# Revit family: NBS_TapcoRoofingProducts_RcnstttdSltCrsngFitngs_TapcoSlate_ClassicRidgeEndCap
name_source: partatom
category: Generic Models
units: mm (PartAtom-declared; Revit-internal decimal feet)

## family parameters
Can host rebar = No
Cut with Voids When Loaded = No
Part Type = Normal
Room Calculation Point = No
Round Connector Dimension = Use Diameter
Shared = No

## types (15) — shared parameters
Applications = Suitable for Tapco Slate Classic and Tapco Slate Classic Ridge and Hip Caps
AssetType = Fixed
Category = Pr_25_93_72_73:Reconstituted slate coursing fittings
ClassicRidgeEndCapHeight = 98 mm  [stored 0.321522 ft]
ClassicRidgeEndCapMaterial = NBS_TapcoRoofingProducts_Slate_706Plum
CodePerformance = Fully tested to BBA, ETA and CE standards
Combustible = Yes
Description = A dry-fix ridge 90° end cap to weather seal and finish the roof line at the end of the ridge, manufactured in the same material as our Tapco Slate Classic product to match the roof slate
DurationUnit = year
ExpectedLife = 80+ years
Features = Lightweight – as low as 12 kg per square metre, easy to install with pre-marked nailing guides and spacers, easily cut with a fine-toothed saw or sharp utility blade, mechanically fixed
FireRating = BS476 Part 3, Boarded Roof SAA, Battened Roof SAC
FlammabilityRating = BS476 Part 3, Boarded Roof SAA, Battened Roof SAC
IfcExportAs = IfcCoveringType
IfcExportType = ROOFING
IsExternal = Yes
ManufacturerName = Tapco Roofing Products
ManufacturerURL = www.tapcoroofingproducts.com
Material = Virgin limestone, polypropylene
NBSCertification = www.nationalbimlibrary.com/cert/mlktdb3y
NBSDescription = Reconstituted slates coursing fittings
NBSReference = 45-80-90/388
NominalHeight = 70 mm
NominalLength = 445 mm  [stored 1.45997 ft]
NominalWidth = 290 mm
ProductInformation = https://www.tapcoroofingproducts.com
Shape = Rectangular
Size = 70 x 445 x 290 mm
Status = UNSET
Uniclass2015Code = Pr_25_93_72_73
Uniclass2015Title = Reconstituted slate coursing fittings
Uniclass2015Version = Products v1.20
Version = 1
WarrantyDescription = 40-years
WarrantyDurationUnit = year
zero-valued in all types: ThermalTransmittance

## per-type parameters (varying)
| type | BIMObjectName | Color | Colour | EndCapPitchAngle | ModelNumber | Name | PitchRange |
| TapcoSlate_ClassicRidgeEndCap_804PewterGrey_25To29DegPitch | NBS_TapcoRoofingProducts_ReconstitutedSlatesCoursingFittings_TapcoSlate_ClassicRidgeEndCap_804PewterGrey_25To29DegPitch | Pewter grey | Pewter grey | 25.00° | 804 | ReconstitutedSlatesCoursingFittings_TapcoSlate_ClassicRidgeEndCap_804PewterGrey_25To29DegPitch_TapcoRoofingProducts | 25° - 29° |
| TapcoSlate_ClassicRidgeEndCap_804PewterGrey30To34DegPitch | NBS_TapcoRoofingProducts_ReconstitutedSlatesCoursingFittings_TapcoSlate_ClassicRidgeEndCap_804PewterGrey30To34DegPitch | Pewter grey | Pewter grey | 30.00° | 804 | ReconstitutedSlatesCoursingFittings_TapcoSlate_ClassicRidgeEndCap_804PewterGrey30To34DegPitch_TapcoRoofingProducts | 30° - 34° |
| TapcoSlate_ClassicRidgeEndCap_804PewterGrey35To40DegPitch | NBS_TapcoRoofingProducts_ReconstitutedSlatesCoursingFittings_TapcoSlate_ClassicRidgeEndCap_804PewterGrey35To40DegPitch | Pewter grey | Pewter grey | 35.00° | 804 | ReconstitutedSlatesCoursingFittings_TapcoSlate_ClassicRidgeEndCap_804PewterGrey35To40DegPitch_TapcoRoofingProducts | 35° - 40° |
| TapcoSlate_ClassicRidgeEndCap_809RedRock_25To29DegPitch | NBS_TapcoRoofingProducts_ReconstitutedSlatesCoursingFittings_TapcoSlate_ClassicRidgeEndCap_809RedRock_25To29DegPitch | Red rock | Red rock | 25.00° | 809 | ReconstitutedSlatesCoursingFittings_TapcoSlate_ClassicRidgeEndCap_809RedRock_25To29DegPitch_TapcoRoofingProducts | 25° - 29° |
| TapcoSlate_ClassicRidgeEndCap_809RedRock_30To34DegPitch | NBS_TapcoRoofingProducts_ReconstitutedSlatesCoursingFittings_TapcoSlate_ClassicRidgeEndCap_809RedRock_30To34DegPitch | Red rock | Red rock | 30.00° | 809 | ReconstitutedSlatesCoursingFittings_TapcoSlate_ClassicRidgeEndCap_809RedRock_30To34DegPitch_TapcoRoofingProducts | 30° - 34° |
| TapcoSlate_ClassicRidgeEndCap_809RedRock_35To40DegPitch | NBS_TapcoRoofingProducts_ReconstitutedSlatesCoursingFittings_TapcoSlate_ClassicRidgeEndCap_809RedRock_35To40DegPitch | Red rock | Red rock | 35.00° | 809 | ReconstitutedSlatesCoursingFittings_TapcoSlate_ClassicRidgeEndCap_809RedRock_35To40DegPitch_TapcoRoofingProducts | 35° - 40° |
| TapcoSlate_ClassicRidgeEndCap_706Plum_25To29DegPitch | NBS_TapcoRoofingProducts_ReconstitutedSlatesCoursingFittings_TapcoSlate_ClassicRidgeEndCap_706Plum_25To29DegPitch | Plum | Plum | 25.00° | 706 | ReconstitutedSlatesCoursingFittings_TapcoSlate_ClassicRidgeEndCap_706Plum_25To29DegPitch_TapcoRoofingProducts | 25° - 29° |
| TapcoSlate_ClassicRidgeEndCap_706Plum_30To34DegPitch | NBS_TapcoRoofingProducts_ReconstitutedSlatesCoursingFittings_TapcoSlate_ClassicRidgeEndCap_706Plum_30To34DegPitch | Plum | Plum | 30.00° | 706 | ReconstitutedSlatesCoursingFittings_TapcoSlate_ClassicRidgeEndCap_706Plum_30To34DegPitch_TapcoRoofingProducts | 30° - 34° |
| TapcoSlate_ClassicRidgeEndCap_706Plum_35To40DegPitch | NBS_TapcoRoofingProducts_ReconstitutedSlatesCoursingFittings_TapcoSlate_ClassicRidgeEndCap_706Plum_35To40DegPitch | Plum | Plum | 35.00° | 706 | ReconstitutedSlatesCoursingFittings_TapcoSlate_ClassicRidgeEndCap_706Plum_35To40DegPitch_TapcoRoofingProducts | 35° - 40° |
| TapcoSlate_ClassicRidgeEndCap_709BrickRed_25To29DegPitch | NBS_TapcoRoofingProducts_ReconstitutedSlatesCoursingFittings_TapcoSlate_ClassicRidgeEndCap_709BrickRed_25To29DegPitch | Brick red | Brick red | 25.00° | 709 | ReconstitutedSlatesCoursingFittings_TapcoSlate_ClassicRidgeEndCap_709BrickRed_25To29DegPitch_TapcoRoofingProducts | 25° - 29° |
| TapcoSlate_ClassicRidgeEndCap_709BrickRed_30To34DegPitch | NBS_TapcoRoofingProducts_ReconstitutedSlatesCoursingFittings_TapcoSlate_ClassicRidgeEndCap_709BrickRed_30To34DegPitch | Brick red | Brick red | 30.00° | 709 | ReconstitutedSlatesCoursingFittings_TapcoSlate_ClassicRidgeEndCap_709BrickRed_30To34DegPitch_TapcoRoofingProducts | 30° - 34° |
| TapcoSlate_ClassicRidgeEndCap_709BrickRed_35To40DegPitch | NBS_TapcoRoofingProducts_ReconstitutedSlatesCoursingFittings_TapcoSlate_ClassicRidgeEndCap_709BrickRed_35To40DegPitch | Brick red | Brick red | 35.00° | 709 | ReconstitutedSlatesCoursingFittings_TapcoSlate_ClassicRidgeEndCap_709BrickRed_35To40DegPitch_TapcoRoofingProducts | 35° - 40° |
| TapcoSlate_ClassicRidgeEndCap_712ChestnutBrown_25To29DegPitch | NBS_TapcoRoofingProducts_ReconstitutedSlatesCoursingFittings_TapcoSlate_ClassicRidgeEndCap_712ChestnutBrown_25To29DegPitch | Chestnut brown | Chestnut brown | 25.00° | 712 | ReconstitutedSlatesCoursingFittings_TapcoSlate_ClassicRidgeEndCap_712ChestnutBrown_25To29DegPitch_TapcoRoofingProducts | 25° - 29° |
| TapcoSlate_ClassicRidgeEndCap_712ChestnutBrown_30To34DegPitch | NBS_TapcoRoofingProducts_ReconstitutedSlatesCoursingFittings_TapcoSlate_ClassicRidgeEndCap_712ChestnutBrown_30To34DegPitch | Chestnut brown | Chestnut brown | 30.00° | 712 | ReconstitutedSlatesCoursingFittings_TapcoSlate_ClassicRidgeEndCap_712ChestnutBrown_30To34DegPitch_TapcoRoofingProducts | 30° - 34° |
| TapcoSlate_ClassicRidgeEndCap_712ChestnutBrown_35To40DegPitch | NBS_TapcoRoofingProducts_ReconstitutedSlatesCoursingFittings_TapcoSlate_ClassicRidgeEndCap_712ChestnutBrown_35To40DegPitch | Chestnut brown | Chestnut brown | 35.00° | 712 | ReconstitutedSlatesCoursingFittings_TapcoSlate_ClassicRidgeEndCap_712ChestnutBrown_35To40DegPitch_TapcoRoofingProducts | 35° - 40° |

note: column(s) folded — value = type name in every type: ModelReference

note: [stored X ft] marks values corroborated as IEEE doubles in the binary element streams (Revit-internal decimal feet)

## geometry (parser evidence)
native form markers: Sweep x3
no freeform markers — native parametric forms only
